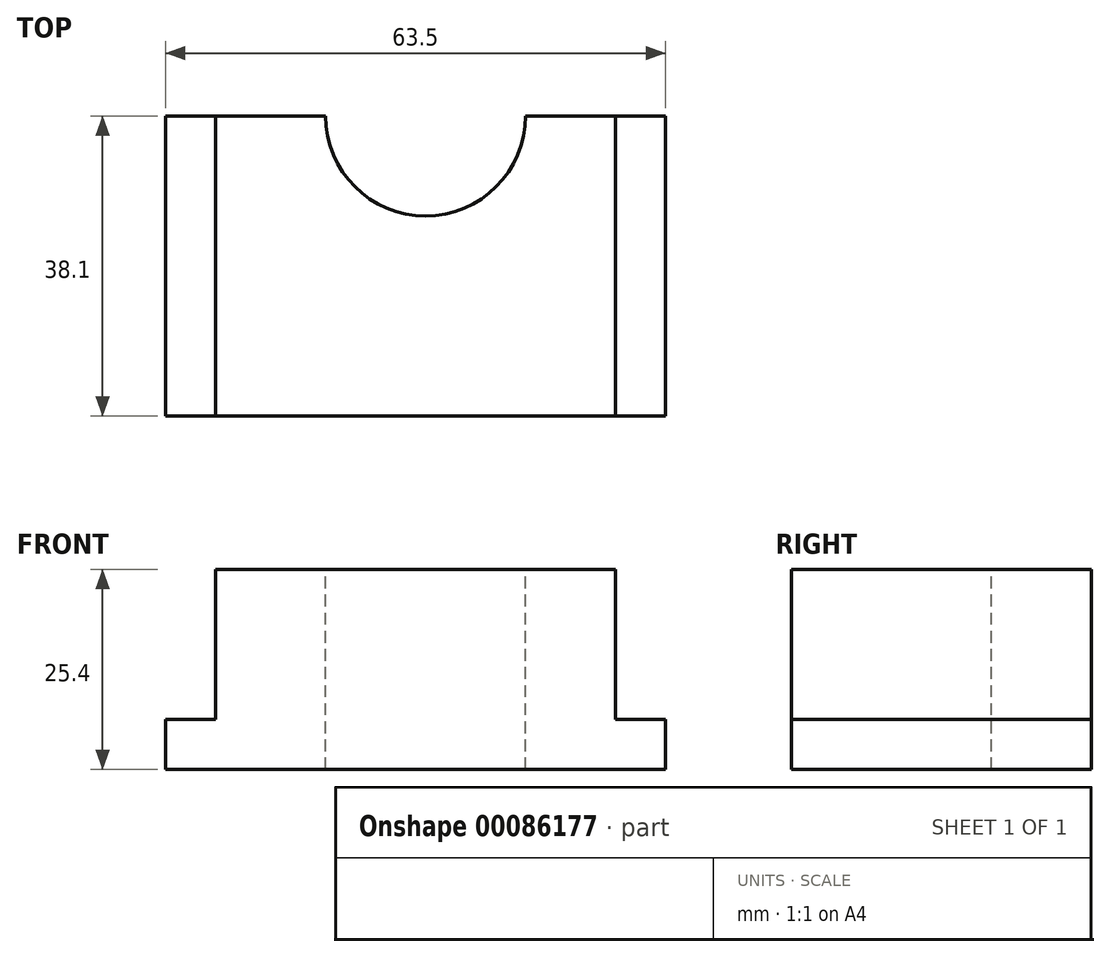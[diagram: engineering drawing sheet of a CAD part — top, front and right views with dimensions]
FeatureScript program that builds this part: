
annotation { "Feature Type Name" : "Feature", "Feature Type Description" : "" }
export const myFeature = defineFeature(function(context is Context, id is Id, definition is map)
    precondition{}
    {
        {
            var Q0;
            Q0=qCreatedBy(makeId("Top.planeOp"),FACE);
            var sketch = newSketch(context, id + "F0", { "sketchPlane" : qUnion([Q0])});
            skLineSegment(sketch, "E0.bottom", {"start": v(-35.96, 19.8) * mm, "end": v(27.54, 19.8) * mm});
            skLineSegment(sketch, "E0.top", {"start": v(-35.96, -18.3) * mm, "end": v(27.54, -18.3) * mm});
            skLineSegment(sketch, "E0.left", {"start": v(-35.96, 19.8) * mm, "end": v(-35.96, -18.3) * mm});
            skLineSegment(sketch, "E0.right", {"start": v(27.54, 19.8) * mm, "end": v(27.54, -18.3) * mm});
            skSolve(sketch);
        }
        {
            var Q0;
            Q0=makeQuery(id+"F0.imprint","IMPRINT",FACE,{"disambiguationData":[TD([[makeQuery(id+"F0.imprint","IMPRINT",EDGE,{"derivedFrom":sQuery(id+"F0.wireOp",EDGE,"E0.bottom")}),-1.0]])]});
            extrude(context, id + "F1", {"entities" : qUnion([Q0]), "depth" : 25.4 * mm});
        }
        {
            var Q0;
            Q0=makeQuery(id+"F1.opExtrude","CAP_FACE",FACE,{"disambiguationData":[OSD([sQuery(id+"F0.wireOp",EDGE,"E0.bottom"),sQuery(id+"F0.wireOp",EDGE,"E0.top"),sQuery(id+"F0.wireOp",EDGE,"E0.left"),sQuery(id+"F0.wireOp",EDGE,"E0.right")])],"isStart":false});
            var sketch = newSketch(context, id + "F2", { "sketchPlane" : qUnion([Q0])});
            skLineSegment(sketch, "E1.bottom", {"start": v(-35.96, 19.8) * mm, "end": v(-29.61, 19.8) * mm});
            skLineSegment(sketch, "E1.top", {"start": v(-35.96, -18.3) * mm, "end": v(-29.61, -18.3) * mm});
            skLineSegment(sketch, "E1.left", {"start": v(-35.96, 19.8) * mm, "end": v(-35.96, -18.3) * mm});
            skLineSegment(sketch, "E1.right", {"start": v(-29.61, 19.8) * mm, "end": v(-29.61, -18.3) * mm});
            skSolve(sketch);
        }
        {
            var Q0;
            Q0=makeQuery(id+"F2.imprint","IMPRINT",FACE,{"disambiguationData":[TD([[makeQuery(id+"F2.imprint","IMPRINT",EDGE,{"derivedFrom":sQuery(id+"F2.wireOp",EDGE,"E1.bottom")}),-1.0]])]});
            extrude(context, id + "F3", {"entities" : qUnion([Q0]), "operationType" : NewBodyOperationType.REMOVE, "oppositeDirection" : true, "depth" : 19.05 * mm});
        }
        {
            var Q0;
            {var subQ0=sQuery(id+"F2.wireOp",EDGE,"E1.right");Q0=makeQuery(id+"F2.imprint","IMPRINT",FACE,{"disambiguationData":[TD([[makeQuery(id+"F2.imprint","IMPRINT",EDGE,{"derivedFrom":subQ0}),1.0]])]});}
            var sketch = newSketch(context, id + "F4", { "sketchPlane" : qUnion([Q0])});
            skSolve(sketch);
        }
        {
            var Q0;
            Q0=makeQuery(id+"F1.opExtrude","SWEPT_FACE",FACE,{"disambiguationData":[OSD([sQuery(id+"F0.wireOp",EDGE,"E0.bottom")])]});
            var sketch = newSketch(context, id + "F5", { "sketchPlane" : qUnion([Q0])});
            skLineSegment(sketch, "E2.bottom", {"start": v(-27.54, 25.4) * mm, "end": v(-21.19, 25.4) * mm});
            skLineSegment(sketch, "E2.top", {"start": v(-27.54, 6.35) * mm, "end": v(-21.19, 6.35) * mm});
            skLineSegment(sketch, "E2.left", {"start": v(-27.54, 25.4) * mm, "end": v(-27.54, 6.35) * mm});
            skLineSegment(sketch, "E2.right", {"start": v(-21.19, 25.4) * mm, "end": v(-21.19, 6.35) * mm});
            skSolve(sketch);
        }
        {
            var Q0;
            Q0=makeQuery(id+"F5.imprint","IMPRINT",FACE,{"disambiguationData":[TD([[makeQuery(id+"F5.imprint","IMPRINT",EDGE,{"derivedFrom":sQuery(id+"F5.wireOp",EDGE,"E2.bottom")}),1.0]])]});
            extrude(context, id + "F6", {"entities" : qUnion([Q0]), "operationType" : NewBodyOperationType.REMOVE, "endBound" : BoundingType.THROUGH_ALL, "oppositeDirection" : true, "depth" : 25.4 * mm});
        }
        {
            var Q0;
            {var subQ0=sQuery(id+"F2.wireOp",EDGE,"E1.right");Q0=makeQuery(id+"F4.imprint","IMPRINT",FACE,{"disambiguationData":[TD([[makeQuery(id+"F4.imprint","IMPRINT",EDGE,{"derivedFrom":makeQuery(id+"F2.imprint","IMPRINT",EDGE,{"derivedFrom":subQ0})}),1.0]])]});}
            var sketch = newSketch(context, id + "F7", { "sketchPlane" : qUnion([Q0])});
            skCircle(sketch, "E3", {"center": v(-2.94, 19.8) * mm, "radius": 12.7 * mm});
            skPoint(sketch, "E3.first.point", {"position": v(-15.64, 19.72) * mm});
            skPoint(sketch, "E3.second.point", {"position": v(9.76, 20.01) * mm});
            skPoint(sketch, "E3.third.point", {"position": v(9.23, 23.44) * mm});
            skSolve(sketch);
        }
        {
            var Q0;
            Q0 = qSketchRegion(id + "F7", true);
            extrude(context, id + "F8", {"entities" : qUnion([Q0]), "operationType" : NewBodyOperationType.REMOVE, "endBound" : BoundingType.THROUGH_ALL, "oppositeDirection" : true, "depth" : 25.4 * mm});
        }
    });
